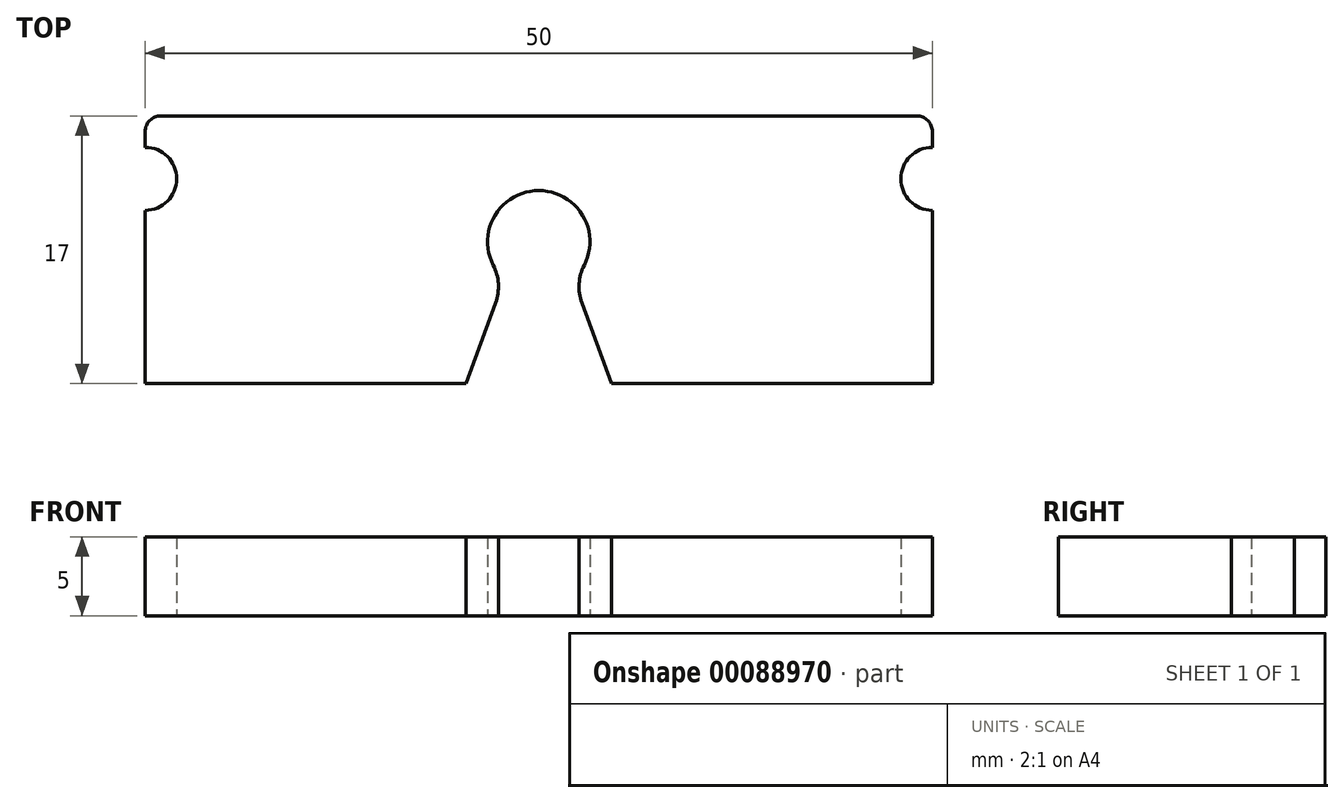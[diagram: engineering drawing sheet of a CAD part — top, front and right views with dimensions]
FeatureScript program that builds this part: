
annotation { "Feature Type Name" : "Feature", "Feature Type Description" : "" }
export const myFeature = defineFeature(function(context is Context, id is Id, definition is map)
    precondition{}
    {
        {
            var Q0;
            Q0=qCreatedBy(makeId("Top.planeOp"),FACE);
            var sketch = newSketch(context, id + "F0", { "sketchPlane" : qUnion([Q0])});
            skArc(sketch, "E0", {"start": v(2.9, -1.48) * mm, "mid": v(0, 3.25) * mm, "end": v(-2.9, -1.48) * mm});
            skLineSegment(sketch, "E1.bottom", {"start": v(-24, 8) * mm, "end": v(24, 8) * mm});
            skLineSegment(sketch, "E1.left", {"start": v(-25, 7) * mm, "end": v(-25, 6) * mm});
            skLineSegment(sketch, "E1.right", {"start": v(25, 7) * mm, "end": v(25, 6) * mm});
            skLineSegment(sketch, "E2", {"start": v(-4.6, -9) * mm, "end": v(-2.74, -3.88) * mm});
            skPoint(sketch, "E3", {"position": v(0, -3.25) * mm});
            skLineSegment(sketch, "E4.MirrorCS", {"start": v(4.6, -9) * mm, "end": v(2.74, -3.88) * mm});
            skPoint(sketch, "E5.visualSharp", {"position": v(-2.2, -2.4) * mm});
            skArc(sketch, "E5.filletArc", {"start": v(-2.74, -3.88) * mm, "mid": v(-2.57, -2.67) * mm, "end": v(-2.9, -1.48) * mm});
            skPoint(sketch, "E6.visualSharp", {"position": v(2.2, -2.4) * mm});
            skArc(sketch, "E6.filletArc", {"start": v(2.9, -1.48) * mm, "mid": v(2.57, -2.67) * mm, "end": v(2.74, -3.88) * mm});
            skArc(sketch, "E7", {"start": v(-25, 2) * mm, "mid": v(-23, 4) * mm, "end": v(-25, 6) * mm});
            skArc(sketch, "E8.MirrorCS", {"start": v(25, 2) * mm, "mid": v(23, 4) * mm, "end": v(25, 6) * mm});
            skPoint(sketch, "E9.visualSharp", {"position": v(-25, 8) * mm});
            skArc(sketch, "E9.filletArc", {"start": v(-24, 8) * mm, "mid": v(-24.7, 7.7) * mm, "end": v(-25, 7) * mm});
            skPoint(sketch, "E10.visualSharp", {"position": v(25, 8) * mm});
            skArc(sketch, "E10.filletArc", {"start": v(25, 7) * mm, "mid": v(24.7, 7.7) * mm, "end": v(24, 8) * mm});
            skLineSegment(sketch, "E11", {"start": v(-25.2, -9) * mm, "end": v(25, -9) * mm, "construction": true});
            skLineSegment(sketch, "E12", {"start": v(-25, 2) * mm, "end": v(-25, -9) * mm});
            skLineSegment(sketch, "E13", {"start": v(-25, -9) * mm, "end": v(-4.6, -9) * mm});
            skLineSegment(sketch, "E14", {"start": v(4.6, -9) * mm, "end": v(25, -9) * mm});
            skLineSegment(sketch, "E15", {"start": v(25, 2) * mm, "end": v(25, -9) * mm});
            skSolve(sketch);
        }
        {
            var Q0;
            Q0=makeQuery(id+"F0.imprint","IMPRINT",FACE,{"disambiguationData":[TD([[makeQuery(id+"F0.imprint","IMPRINT",EDGE,{"derivedFrom":sQuery(id+"F0.wireOp",EDGE,"E0")}),-1.0]])]});
            extrude(context, id + "F1", {"entities" : qUnion([Q0]), "depth" : 5 * mm});
        }
    });
